# Revit family: EC2N
name_source: partatom
category: Lighting Fixtures
revit_build: Autodesk Revit 2014 (Build: 20130308_1515(x64)
units: mm (PartAtom-declared; Revit-internal decimal feet)

## types (1)
- EC2N
    Apparent Load = 50 VA
    Assembly Code = D5020200
    Color Filter = 16777215
    Connector Description = Lighting Connector
    Default Elevation = 1219.2 mm  [stored 4 ft]
    Description = The Eclipse II wellglass has been designed to make installation quick and simple. The lamp and gear chambers are separated for easy maintenance and require no special cable glands. The luminaire also features a swing barrel nut system. This allows prior installation and wiring of the mounting base without the need to support the body and lamps. This unique design saves on both time and labour costs.
    Dimming Lamp Color Temperature Shift = <None>
    Emit Shape Visible in Rendering = No
    Emit from Circle Diameter = 50 mm  [stored 0.164042 ft]
    Features = Easy access for wiring and control gear.
Unrestricted breathing gear enclosure removes the need for special glands or cable.
Corrosion resistant.
High, medium and low bay lighting.
Excellent light distribution.
Suitable for a wide range of ambient temperatures from -30°C to +55°C, dependant on lamp type and wattage.
Option available for Zone 22 combustable dust environments.
ATEX Certified, GOST R Approved and IECEx Compliant.
    Fixture distribution = Direct
    Glass = Hubbell - Glass
    Height = 535 mm
    Housing Material = Paint- Hubbell- Yellow
    IP Rating = IP66/67
    Inner Length = 200 mm  [stored 0.656168 ft]
    Lamp = LED
    Length = 245 mm  [stored 0.803806 ft]
    Load Classification = Lighting
    Manufacturer = Chalmit
    Model = EC2N
    Mounting = Paint - Hubbell - Light Silver
    Photometric Web File = CHL_EC2N_050_HS.ies
    Power Factor = 1
    Product Documentation Link = https://hubbellcdn.com
    Product Link = https://www.hubbell.com
    Reflector Finish = Hubbell - White Glass
    Tilt Angle = 90.00°
    URL = https://www.hubbell.com
    Voltage = 120 V
    Warranty = 5 years Warranty
    Wattage Comments = 50W
    Watts = 50 W
    Width = 280 mm  [stored 0.918635 ft]
    Wings = Paint - Hubbell - Light Silver

note: [stored X ft] marks values corroborated as IEEE doubles in the binary element streams (Revit-internal decimal feet)

## geometry (parser evidence)
native form markers: Sweep x4
no freeform markers — native parametric forms only
